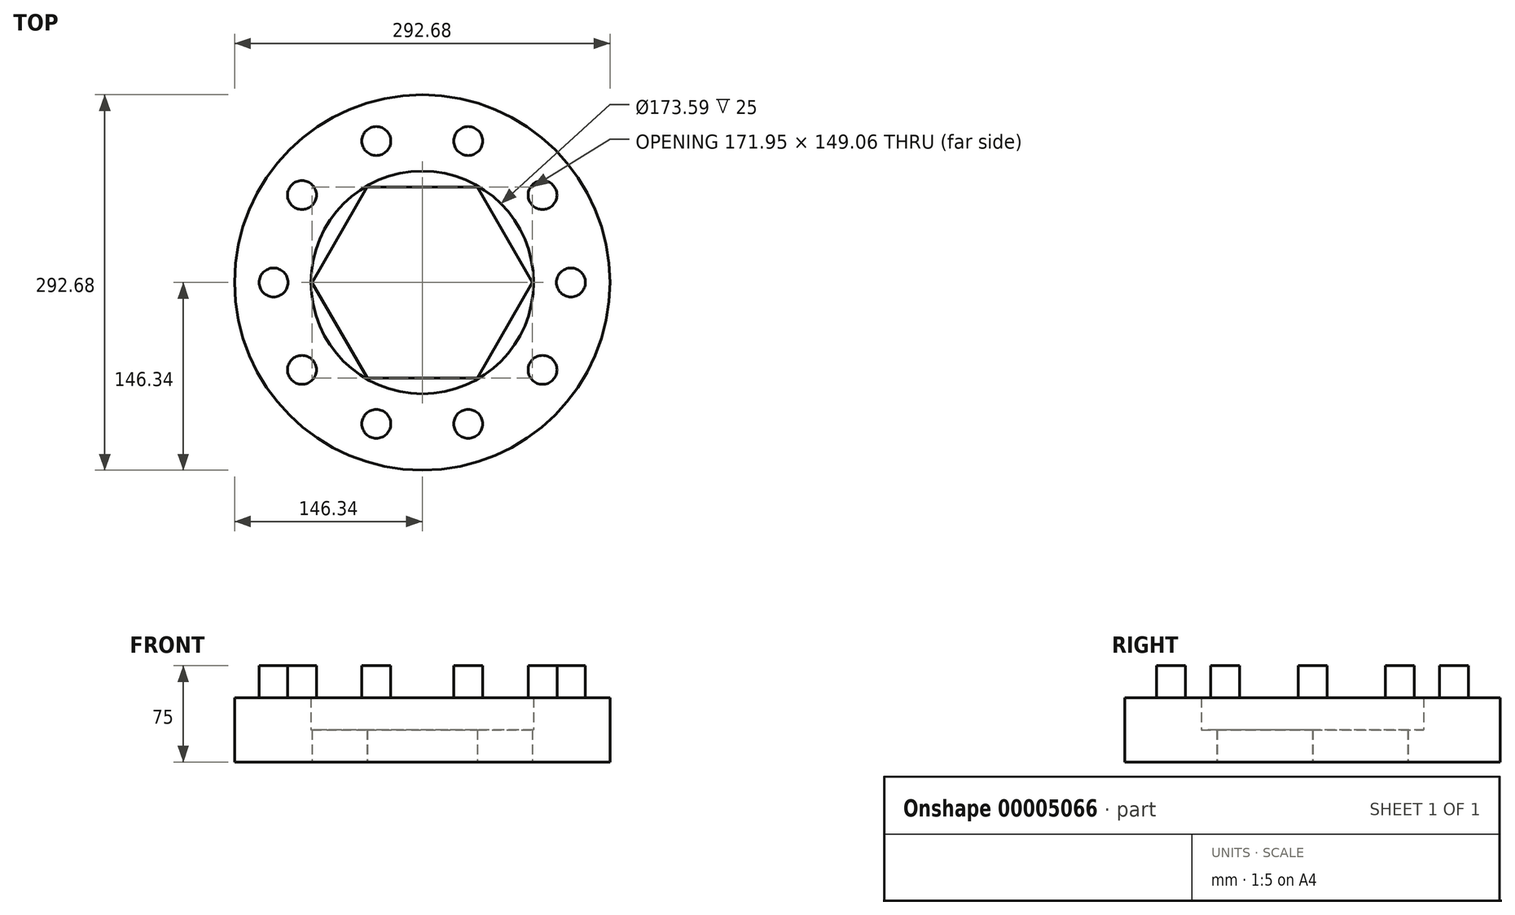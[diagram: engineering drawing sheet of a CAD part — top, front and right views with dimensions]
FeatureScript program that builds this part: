
annotation { "Feature Type Name" : "Feature", "Feature Type Description" : "" }
export const myFeature = defineFeature(function(context is Context, id is Id, definition is map)
    precondition{}
    {
        {
            var Q0;
            Q0=qCreatedBy(makeId("Top.planeOp"),FACE);
            var sketch = newSketch(context, id + "F0", { "sketchPlane" : qUnion([Q0])});
            skCircle(sketch, "E0", {"center": v(0, 0) * mm, "radius": 146.34 * mm});
            skCircle(sketch, "E1.cCircle", {"center": v(0, 0) * mm, "radius": 74.46 * mm, "construction": true});
            skLineSegment(sketch, "E1.0", {"start": v(85.97, 0.15) * mm, "end": v(43.12, -74.38) * mm});
            skLineSegment(sketch, "E1.1", {"start": v(43.12, -74.38) * mm, "end": v(-42.86, -74.53) * mm});
            skLineSegment(sketch, "E1.2", {"start": v(-42.86, -74.53) * mm, "end": v(-85.97, -0.15) * mm});
            skLineSegment(sketch, "E1.3", {"start": v(-85.97, -0.15) * mm, "end": v(-43.12, 74.38) * mm});
            skLineSegment(sketch, "E1.4", {"start": v(-43.12, 74.38) * mm, "end": v(42.86, 74.53) * mm});
            skLineSegment(sketch, "E1.5", {"start": v(42.86, 74.53) * mm, "end": v(85.97, 0.15) * mm});
            skPoint(sketch, "E1.0.midPoint", {"position": v(64.54, -37.12) * mm});
            skSolve(sketch);
        }
        {
            var Q0;
            Q0=qSketchRegion(id+"F0",true);
            extrude(context, id + "F1", {"entities" : qUnion([Q0]), "depth" : 25 * mm});
        }
        {
            var Q0;
            Q0=makeQuery(id+"F1.opExtrude","CAP_FACE",FACE,{"disambiguationData":[OSD([sQuery(id+"F0.wireOp",EDGE,"E0"),sQuery(id+"F0.wireOp",EDGE,"E1.0"),sQuery(id+"F0.wireOp",EDGE,"E1.1"),sQuery(id+"F0.wireOp",EDGE,"E1.2"),sQuery(id+"F0.wireOp",EDGE,"E1.3"),sQuery(id+"F0.wireOp",EDGE,"E1.4"),sQuery(id+"F0.wireOp",EDGE,"E1.5")])],"isStart":false});
            var sketch = newSketch(context, id + "F2", { "sketchPlane" : qUnion([Q0])});
            skCircle(sketch, "E2", {"center": v(0, 0) * mm, "radius": 86.8 * mm});
            skSolve(sketch);
        }
        {
            var Q0;
            Q0=makeQuery(id+"F2.imprint","IMPRINT",FACE,{"disambiguationData":[TD([[makeQuery(id+"F2.imprint","IMPRINT",EDGE,{"derivedFrom":sQuery(id+"F2.wireOp",EDGE,"E2")}),-1.0]])]});
            extrude(context, id + "F3", {"entities" : qUnion([Q0]), "operationType" : NewBodyOperationType.ADD, "depth" : 25 * mm});
        }
        {
            var Q0;
            Q0=makeQuery(id+"F3.opExtrude","CAP_FACE",FACE,{"disambiguationData":[OSD([sQuery(id+"F0.wireOp",EDGE,"E0"),sQuery(id+"F2.wireOp",EDGE,"E2")])],"isStart":false});
            var sketch = newSketch(context, id + "F4", { "sketchPlane" : qUnion([Q0])});
            skCircle(sketch, "E3", {"center": v(-115.93, 0) * mm, "radius": 11.28 * mm});
            skSolve(sketch);
        }
        {
            var Q0;
            Q0=qSketchRegion(id+"F4",true);
            extrude(context, id + "F5", {"entities" : qUnion([Q0]), "depth" : 25 * mm});
        }
        {
            var Q0;
            Q0=makeQuery(id+"F5.opExtrude","SWEPT_BODY",BODY,{"disambiguationData":[OSD([sQuery(id+"F4.wireOp",EDGE,"E3")])]});
            var Q1;
            Q1=makeQuery(id+"F3.opExtrude","CAP_EDGE",EDGE,{"disambiguationData":[OSD([sQuery(id+"F0.wireOp",EDGE,"E0")])],"isStart":false});
            circularPattern(context, id + "F6", {"entities" : qUnion([Q0]), "axis" : qUnion([Q1]), "angle" : 360 * degree, "instanceCount" : round(10), "equalSpace" : true});
        }
    });
